# Revit family: Franke_A200_FM_CM_Tank
name_source: partatom
category: Sonderausstattung
revit_build: Autodesk Revit 2015 (Build: 20140606_1530(x64)
units: mm (PartAtom-declared; Revit-internal decimal feet)

## types (2) — shared parameters
Anzahl Pole (A200) = 1
Anzahl Pole (SU05) = 1
Anzahl der Nullleiter (A200) = 1
Anzahl der Nullleiter (SU05) = 1
Anzahl der Schutzleiter (A200) = 1
Anzahl der Schutzleiter (SU05) = 1
Aufstellgewicht = 50 kg
Bauelement = Kaffeevollautomat
Baugruppenkennzeichen = Kaffeevollautomat
Beschreibung = A200 Kaffeevollautomat mit 2 geräuscharmen Präzisionskaffeemühlen incl. Kühleinheit SU05 FM1
Breite = 613 mm  [stored 2.01115 ft]
Energieverlust nach DIN18873(A200 FM inkl. SU05 FM) = 1,105 kWh/24h - 230 V
Hersteller = Franke
Höhe = 604 mm  [stored 1.98163 ft]
Leistung max. (A200) = 2750 W
Leistung max. (SU05) = 2300 W
Leistung min. (A200) = 2400 W
Leistung min. (SU05) = 1950 W
Milchvorrat (SU05) = 5 l
Modell = 410914 - A200 FM CM Tank
Netzfrequenz (A200) = 50 Hz
Netzfrequenz (SU05) = 50 Hz
Netzfrequenz alternativ (A200) = 60 Hz
Netzfrequenz alternativ (SU05) = 60 Hz
Schallemission = 70 dB
Sicherung (A200) = 16 A
Sicherung (SU05) = 10 A
Spannung max. (A200) = 240 V
Spannung max. (SU05) = 240 V
Spannung min. (A200) = 220 V
Spannung min. (SU05) = 220 V
Temperaturbereich = 3° - 8°
Tiefe = 560 mm  [stored 1.83727 ft]
URL = http://www.franke.com
Wassertank intern = 4,0 l
zero-valued in all types: Kosten

## per-type parameters (varying)
| type | Abdeckung Front |
| A200 FM CM Tank(220-240V/black line/EU) | Franke Black |
| A200 FM CM Tank(220-240V/anthrazit/EU) | Franke Anthrazit |

note: [stored X ft] marks values corroborated as IEEE doubles in the binary element streams (Revit-internal decimal feet)
